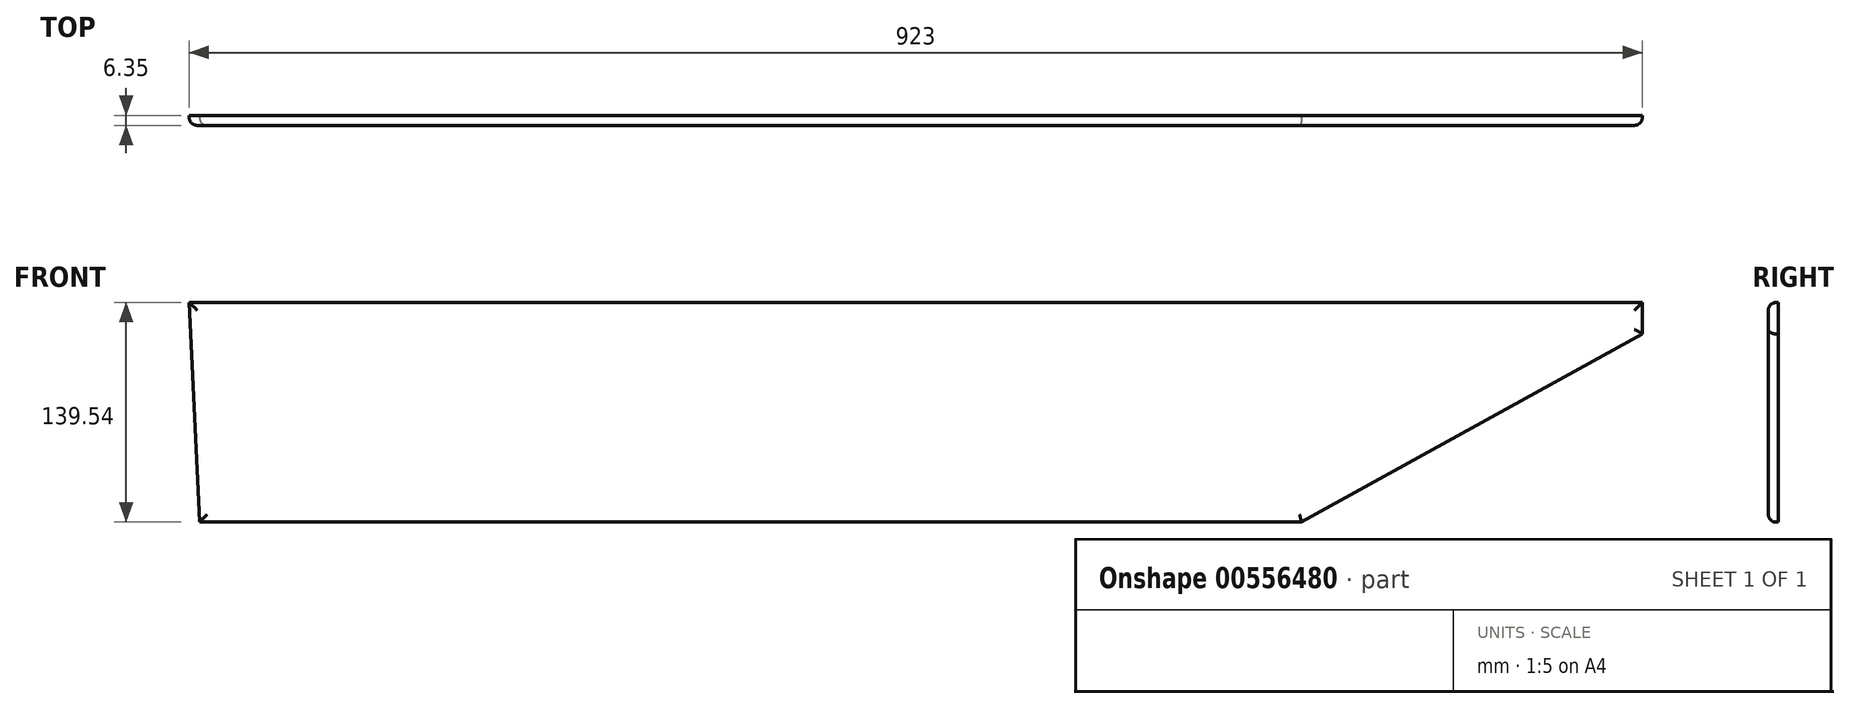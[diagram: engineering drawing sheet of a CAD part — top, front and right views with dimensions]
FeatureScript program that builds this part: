
annotation { "Feature Type Name" : "Feature", "Feature Type Description" : "" }
export const myFeature = defineFeature(function(context is Context, id is Id, definition is map)
    precondition{}
    {
        {
            var Q0;
            Q0=qCreatedBy(makeId("Front.planeOp"),FACE);
            var sketch = newSketch(context, id + "F0", { "sketchPlane" : qUnion([Q0])});
            skLineSegment(sketch, "E0", {"start": v(-550.34, 966.67) * mm, "end": v(372.66, 966.67) * mm});
            skLineSegment(sketch, "E1", {"start": v(156.24, 827.13) * mm, "end": v(-543.76, 827.13) * mm});
            skLineSegment(sketch, "E2", {"start": v(-543.76, 827.13) * mm, "end": v(-550.34, 966.67) * mm});
            skLineSegment(sketch, "E3", {"start": v(372.66, 966.67) * mm, "end": v(372.66, 946.67) * mm});
            skLineSegment(sketch, "E4", {"start": v(372.66, 946.67) * mm, "end": v(156.24, 827.13) * mm});
            skSolve(sketch);
        }
        {
            var Q0;
            Q0 = qSketchRegion(id + "F0", true);
            extrude(context, id + "F1", {"entities" : qUnion([Q0]), "depth" : 6.35 * mm, "offsetDistance" : 25 * mm});
        }
        {
            var Q0;
            Q0=makeQuery(id+"F1.opExtrude","CAP_FACE",FACE,{"disambiguationData":[OSD([sQuery(id+"F0.wireOp",EDGE,"E0"),sQuery(id+"F0.wireOp",EDGE,"E1"),sQuery(id+"F0.wireOp",EDGE,"E2"),sQuery(id+"F0.wireOp",EDGE,"E3"),sQuery(id+"F0.wireOp",EDGE,"E4")])],"isStart":false});
            var Q1;
            Q1=makeQuery(id+"F1.opExtrude","CAP_EDGE",EDGE,{"disambiguationData":[OSD([sQuery(id+"F0.wireOp",EDGE,"E0")])],"isStart":false});
            var Q2;
            Q2=makeQuery(id+"F1.opExtrude","CAP_EDGE",EDGE,{"disambiguationData":[OSD([sQuery(id+"F0.wireOp",EDGE,"E2")])],"isStart":false});
            var Q3;
            Q3=makeQuery(id+"F1.opExtrude","CAP_EDGE",EDGE,{"disambiguationData":[OSD([sQuery(id+"F0.wireOp",EDGE,"E1")])],"isStart":false});
            var Q4;
            Q4=makeQuery(id+"F1.opExtrude","CAP_EDGE",EDGE,{"disambiguationData":[OSD([sQuery(id+"F0.wireOp",EDGE,"E4")])],"isStart":false});
            fillet(context, id + "F2", {"entities" : qUnion([Q0, Q1, Q2, Q3, Q4]), "radius" : 5 * mm, "tangentPropagation" : true, "allowEdgeOverflow" : false});
        }
    });
